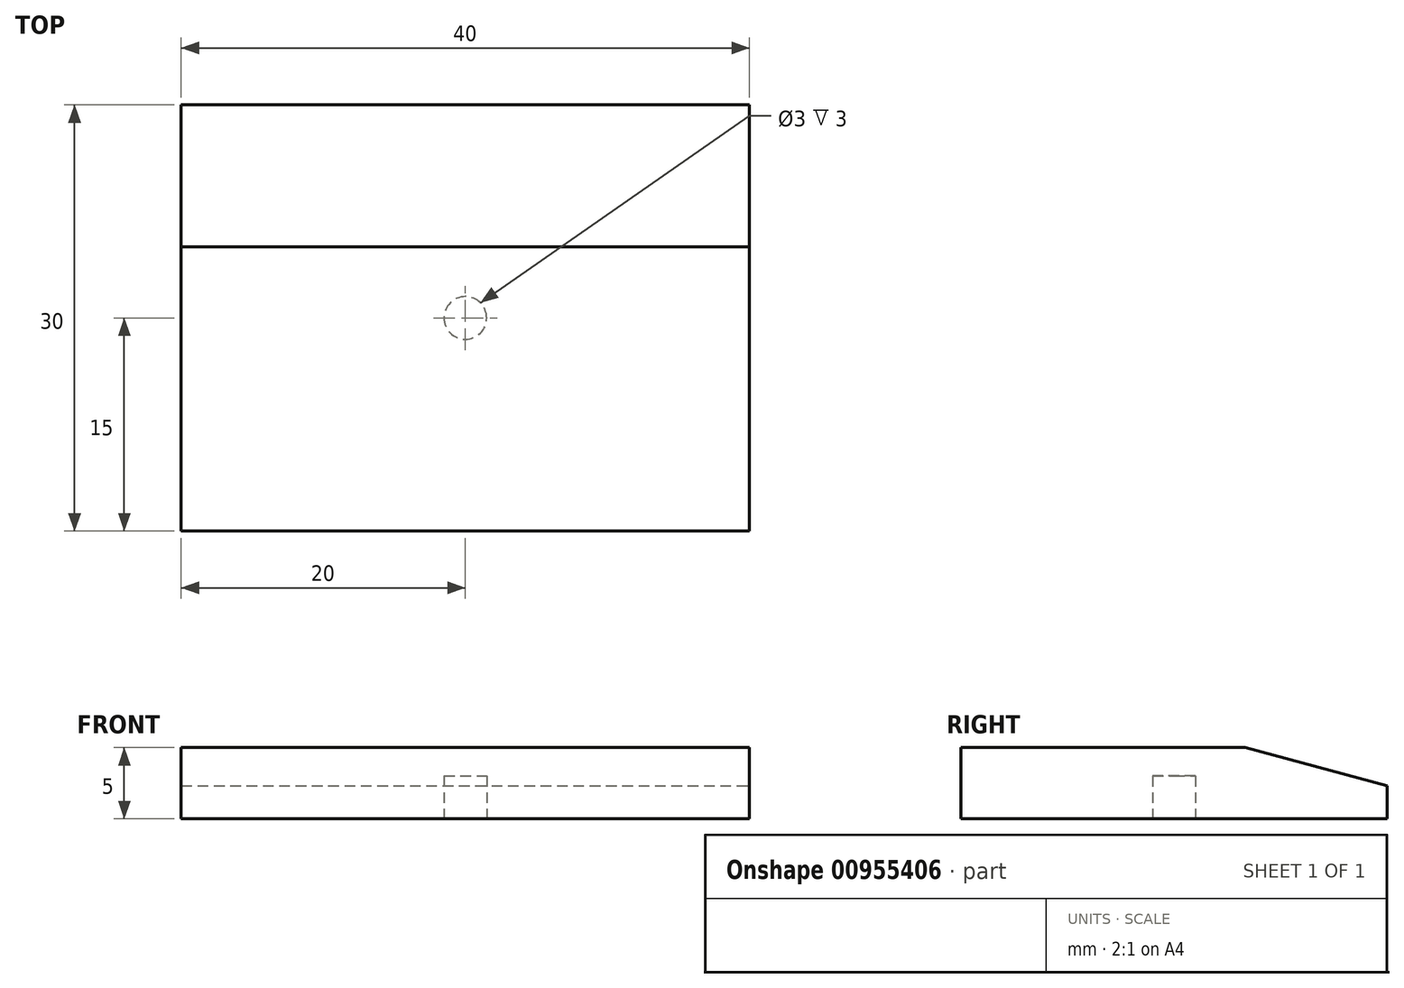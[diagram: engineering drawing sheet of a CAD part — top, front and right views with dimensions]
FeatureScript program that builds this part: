
annotation { "Feature Type Name" : "Feature", "Feature Type Description" : "" }
export const myFeature = defineFeature(function(context is Context, id is Id, definition is map)
    precondition{}
    {
        {
            var Q0;
            Q0=qCreatedBy(makeId("Top.planeOp"),FACE);
            var sketch = newSketch(context, id + "F0", { "sketchPlane" : qUnion([Q0])});
            skCircle(sketch, "E0", {"center": v(0, 0) * mm, "radius": 1.25 * mm});
            skSolve(sketch);
        }
        {
            var Q0;
            Q0 = qSketchRegion(id + "F0", true);
            extrude(context, id + "F1", {"entities" : qUnion([Q0]), "depth" : 5 * mm, "offsetDistance" : 25 * mm});
        }
        {
            var Q0;
            Q0=makeQuery(id+"F1.opExtrude","CAP_FACE",FACE,{"disambiguationData":[OSD([sQuery(id+"F0.wireOp",EDGE,"E0")])],"isStart":false});
            var sketch = newSketch(context, id + "F2", { "sketchPlane" : qUnion([Q0])});
            skLineSegment(sketch, "E1.bottom", {"start": v(20, -15) * mm, "end": v(-20, -15) * mm});
            skLineSegment(sketch, "E1.top", {"start": v(20, 15) * mm, "end": v(-20, 15) * mm});
            skLineSegment(sketch, "E1.left", {"start": v(20, -15) * mm, "end": v(20, 15) * mm});
            skLineSegment(sketch, "E1.right", {"start": v(-20, -15) * mm, "end": v(-20, 15) * mm});
            skPoint(sketch, "E1.middle", {"position": v(0, 0) * mm});
            skSolve(sketch);
        }
        {
            var Q0;
            Q0 = qSketchRegion(id + "F2", true);
            extrude(context, id + "F3", {"entities" : qUnion([Q0]), "operationType" : NewBodyOperationType.ADD, "depth" : 5 * mm, "offsetDistance" : 25 * mm});
        }
        {
            var Q0;
            Q0=makeQuery(id+"F3.opExtrude","CAP_EDGE",EDGE,{"disambiguationData":[OSD([sQuery(id+"F2.wireOp",EDGE,"E1.top")])],"isStart":false});
            chamfer(context, id + "F4", {"entities" : qUnion([Q0]), "chamferType" : ChamferType.OFFSET_ANGLE, "width" : 10 * mm, "oppositeDirection" : false, "angle" : 15 * degree, "tangentPropagation" : true});
        }
        {
            var Q0;
            Q0=makeQuery(id+"F1.opExtrude","CAP_FACE",FACE,{"disambiguationData":[OSD([sQuery(id+"F0.wireOp",EDGE,"E0")])],"isStart":true});
            extrude(context, id + "F5", {"entities" : qUnion([Q0]), "operationType" : NewBodyOperationType.REMOVE, "oppositeDirection" : true, "depth" : 5 * mm, "offsetDistance" : 25 * mm});
        }
        {
            var Q0;
            Q0=makeQuery(id+"F5.boolean.opBoolean","MERGE",FACE,{"derivedFrom":[makeQuery(id+"F3.opExtrude","CAP_FACE",FACE,{"disambiguationData":[OSD([sQuery(id+"F2.wireOp",EDGE,"E1.bottom"),sQuery(id+"F2.wireOp",EDGE,"E1.top"),sQuery(id+"F2.wireOp",EDGE,"E1.left"),sQuery(id+"F2.wireOp",EDGE,"E1.right")])],"isStart":true})],"fromTools":[makeQuery(id+"F5.opExtrude","CAP_FACE",FACE,{"disambiguationData":[OSD([sQuery(id+"F0.wireOp",EDGE,"E0")])],"isStart":false})]});
            var sketch = newSketch(context, id + "F6", { "sketchPlane" : qUnion([Q0])});
            skCircle(sketch, "E2", {"center": v(0, 0) * mm, "radius": 1.5 * mm});
            skSolve(sketch);
        }
        {
            var Q0;
            Q0 = qSketchRegion(id + "F6", true);
            extrude(context, id + "F7", {"entities" : qUnion([Q0]), "operationType" : NewBodyOperationType.REMOVE, "oppositeDirection" : true, "depth" : 3 * mm, "offsetDistance" : 25 * mm});
        }
    });
